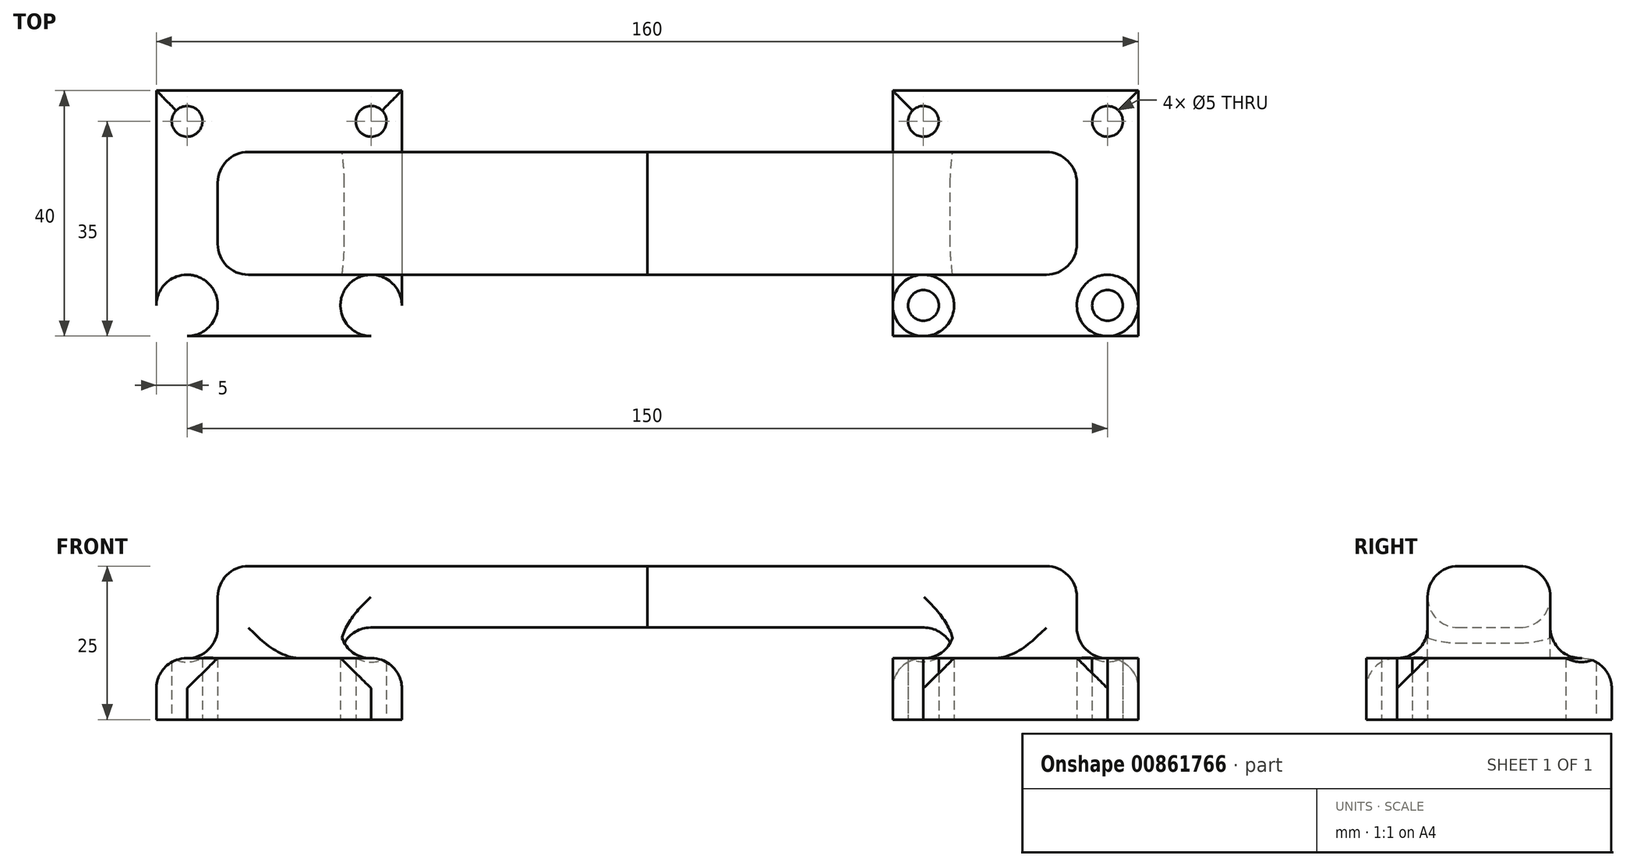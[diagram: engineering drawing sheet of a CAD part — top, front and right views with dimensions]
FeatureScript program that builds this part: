
annotation { "Feature Type Name" : "Feature", "Feature Type Description" : "" }
export const myFeature = defineFeature(function(context is Context, id is Id, definition is map)
    precondition{}
    {
        {
            var Q0;
            Q0=qCreatedBy(makeId("Top.planeOp"),FACE);
            var sketch = newSketch(context, id + "F0", { "sketchPlane" : qUnion([Q0])});
            skLineSegment(sketch, "E0", {"start": v(0, 90.84) * mm, "end": v(0, -111.33) * mm, "construction": true});
            skLineSegment(sketch, "E1.bottom", {"start": v(40, 20) * mm, "end": v(80, 20) * mm});
            skLineSegment(sketch, "E1.top", {"start": v(40, -20) * mm, "end": v(80, -20) * mm});
            skLineSegment(sketch, "E1.left", {"start": v(40, 20) * mm, "end": v(40, -20) * mm});
            skLineSegment(sketch, "E1.right", {"start": v(80, 20) * mm, "end": v(80, -20) * mm});
            skLineSegment(sketch, "E2.bottom", {"start": v(70, -10) * mm, "end": v(50, -10) * mm});
            skLineSegment(sketch, "E2.top", {"start": v(70, 10) * mm, "end": v(50, 10) * mm});
            skLineSegment(sketch, "E2.left", {"start": v(70, -10) * mm, "end": v(70, 10) * mm});
            skLineSegment(sketch, "E2.right", {"start": v(50, -10) * mm, "end": v(50, 10) * mm});
            skLineSegment(sketch, "E3.bottom", {"start": v(70, -10) * mm, "end": v(0, -10) * mm});
            skLineSegment(sketch, "E3.top", {"start": v(70, 10) * mm, "end": v(0, 10) * mm});
            skLineSegment(sketch, "E3.right", {"start": v(0, -10) * mm, "end": v(0, 10) * mm});
            skPoint(sketch, "E4", {"position": v(80, 0) * mm});
            skPoint(sketch, "E5", {"position": v(70, 0) * mm});
            skLineSegment(sketch, "E6", {"start": v(40, 20) * mm, "end": v(50, 10) * mm, "construction": true});
            skLineSegment(sketch, "E7", {"start": v(70, 10) * mm, "end": v(80, 20) * mm, "construction": true});
            skLineSegment(sketch, "E8", {"start": v(70, -10) * mm, "end": v(80, -20) * mm, "construction": true});
            skLineSegment(sketch, "E9", {"start": v(50, -10) * mm, "end": v(40, -20) * mm, "construction": true});
            skPoint(sketch, "E10", {"position": v(75, 15) * mm});
            skPoint(sketch, "E11", {"position": v(45, 15) * mm});
            skPoint(sketch, "E12", {"position": v(45, -15) * mm});
            skPoint(sketch, "E13", {"position": v(75, -15) * mm});
            skCircle(sketch, "E14", {"center": v(45, 15) * mm, "radius": 5 * mm});
            skCircle(sketch, "E15", {"center": v(45, 15) * mm, "radius": 2.5 * mm});
            skCircle(sketch, "E16.MirrorC", {"center": v(75, -15) * mm, "radius": 2.5 * mm});
            skCircle(sketch, "E17.MirrorC", {"center": v(75, -15) * mm, "radius": 5 * mm});
            skLineSegment(sketch, "E18", {"start": v(0, 0) * mm, "end": v(96.53, 0) * mm, "construction": true});
            skCircle(sketch, "E19.MirrorC", {"center": v(45, -15) * mm, "radius": 2.5 * mm});
            skCircle(sketch, "E20.MirrorC", {"center": v(45, -15) * mm, "radius": 5 * mm});
            skCircle(sketch, "E21.MirrorC", {"center": v(75, 15) * mm, "radius": 5 * mm});
            skCircle(sketch, "E22.MirrorC", {"center": v(75, 15) * mm, "radius": 2.5 * mm});
            skSolve(sketch);
        }
        {
            var Q0;
            {var subQ4=sQuery(id+"F0.wireOp",EDGE,"E1.bottom");Q0=makeQuery(id+"F0.imprint","IMPRINT",FACE,{"disambiguationData":[TD([[makeQuery(id+"F0.imprint","IMPRINT",EDGE,{"derivedFrom":subQ4}),-1.0]])]});}
            var Q1;
            {var subQ5=sQuery(id+"F0.wireOp",EDGE,"E2.right");Q1=makeQuery(id+"F0.imprint","IMPRINT",FACE,{"disambiguationData":[TD([[makeQuery(id+"F0.imprint","IMPRINT",EDGE,{"derivedFrom":subQ5}),1.0]])]});}
            var Q2;
            {var subQ0=sQuery(id+"F0.wireOp",EDGE,"E2.right");Q2=makeQuery(id+"F0.imprint","IMPRINT",FACE,{"disambiguationData":[TD([[makeQuery(id+"F0.imprint","IMPRINT",EDGE,{"derivedFrom":subQ0}),-1.0]])]});}
            var Q3;
            {var subQ10=sQuery(id+"F0.wireOp",EDGE,"E2.left");Q3=makeQuery(id+"F0.imprint","IMPRINT",FACE,{"disambiguationData":[TD([[makeQuery(id+"F0.imprint","IMPRINT",EDGE,{"derivedFrom":subQ10}),-1.0]])]});}
            var Q4;
            Q4=makeQuery(id+"F0.imprint","IMPRINT",FACE,{"disambiguationData":[TD([[makeQuery(id+"F0.imprint","IMPRINT",EDGE,{"derivedFrom":sQuery(id+"F0.wireOp",EDGE,"E15")}),-1.0]])]});
            var Q5;
            Q5=makeQuery(id+"F0.imprint","IMPRINT",FACE,{"disambiguationData":[TD([[makeQuery(id+"F0.imprint","IMPRINT",EDGE,{"derivedFrom":sQuery(id+"F0.wireOp",EDGE,"E22.MirrorC")}),-1.0]])]});
            var Q6;
            Q6=makeQuery(id+"F0.imprint","IMPRINT",FACE,{"disambiguationData":[TD([[makeQuery(id+"F0.imprint","IMPRINT",EDGE,{"derivedFrom":sQuery(id+"F0.wireOp",EDGE,"E16.MirrorC")}),1.0]])]});
            var Q7;
            Q7=makeQuery(id+"F0.imprint","IMPRINT",FACE,{"disambiguationData":[TD([[makeQuery(id+"F0.imprint","IMPRINT",EDGE,{"derivedFrom":sQuery(id+"F0.wireOp",EDGE,"E19.MirrorC")}),1.0]])]});
            var Q8;
            {var subQ0=sQuery(id+"F0.wireOp",EDGE,"E3.bottom");var subQ1=sQuery(id+"F0.wireOp",EDGE,"E1.left");var subQ2=makeQuery(id+"F0.imprint","INTERSECT",VERTEX,{"derivedFrom":[subQ1,subQ0]});Q8=makeQuery(id+"F0.imprint","IMPRINT",FACE,{"disambiguationData":[TD([[makeQuery(id+"F0.imprint","IMPRINT",EDGE,{"disambiguationData":[TD([[subQ2,-1.0]])],"derivedFrom":subQ1}),1.0]])]});}
            var Q9;
            {var subQ0=sQuery(id+"F0.wireOp",EDGE,"E14");var subQ1=sQuery(id+"F0.wireOp",EDGE,"E1.left");var subQ2=makeQuery(id+"F0.imprint","INTERSECT",VERTEX,{"derivedFrom":[subQ1,subQ0]});Q9=makeQuery(id+"F0.imprint","IMPRINT",FACE,{"disambiguationData":[TD([[makeQuery(id+"F0.imprint","IMPRINT",EDGE,{"disambiguationData":[TD([[subQ2,-1.0]])],"derivedFrom":subQ1}),1.0]])]});}
            var Q10;
            {var subQ0=sQuery(id+"F0.wireOp",EDGE,"E1.left");var subQ1=sQuery(id+"F0.wireOp",EDGE,"E1.top");var subQ2=makeQuery(id+"F0.imprint","INTERSECT",VERTEX,{"derivedFrom":[subQ1,subQ0]});Q10=makeQuery(id+"F0.imprint","IMPRINT",FACE,{"disambiguationData":[TD([[makeQuery(id+"F0.imprint","IMPRINT",EDGE,{"disambiguationData":[TD([[subQ2,-1.0]])],"derivedFrom":subQ1}),1.0]])]});}
            var Q11;
            {var subQ0=sQuery(id+"F0.wireOp",EDGE,"E1.right");var subQ1=sQuery(id+"F0.wireOp",EDGE,"E1.top");var subQ2=makeQuery(id+"F0.imprint","INTERSECT",VERTEX,{"derivedFrom":[subQ1,subQ0]});Q11=makeQuery(id+"F0.imprint","IMPRINT",FACE,{"disambiguationData":[TD([[makeQuery(id+"F0.imprint","IMPRINT",EDGE,{"disambiguationData":[TD([[subQ2,1.0]])],"derivedFrom":subQ1}),1.0]])]});}
            extrude(context, id + "F1", {"entities" : qUnion([Q0, Q1, Q2, Q3, Q4, Q5, Q6, Q7, Q8, Q9, Q10, Q11]), "depth" : 10 * mm, "offsetDistance" : 25 * mm});
        }
        {
            var Q0;
            {var subQ0=sQuery(id+"F0.wireOp",EDGE,"E2.right");Q0=makeQuery(id+"F0.imprint","IMPRINT",FACE,{"disambiguationData":[TD([[makeQuery(id+"F0.imprint","IMPRINT",EDGE,{"derivedFrom":subQ0}),-1.0]])]});}
            extrude(context, id + "F2", {"entities" : qUnion([Q0]), "operationType" : NewBodyOperationType.ADD, "depth" : 25 * mm, "offsetDistance" : 25 * mm});
        }
        {
            var Q0;
            {var subQ5=sQuery(id+"F0.wireOp",EDGE,"E3.right");Q0=makeQuery(id+"F0.imprint","IMPRINT",FACE,{"disambiguationData":[TD([[makeQuery(id+"F0.imprint","IMPRINT",EDGE,{"derivedFrom":subQ5}),-1.0]])]});}
            var Q1;
            {var subQ5=sQuery(id+"F0.wireOp",EDGE,"E2.right");Q1=makeQuery(id+"F0.imprint","IMPRINT",FACE,{"disambiguationData":[TD([[makeQuery(id+"F0.imprint","IMPRINT",EDGE,{"derivedFrom":subQ5}),1.0]])]});}
            var Q2;
            {var subQ0=sQuery(id+"F0.wireOp",EDGE,"E2.right");Q2=makeQuery(id+"F0.imprint","IMPRINT",FACE,{"disambiguationData":[TD([[makeQuery(id+"F0.imprint","IMPRINT",EDGE,{"derivedFrom":subQ0}),-1.0]])]});}
            extrude(context, id + "F3", {"entities" : qUnion([Q0, Q1, Q2]), "operationType" : NewBodyOperationType.ADD, "depth" : 25 * mm, "offsetDistance" : 25 * mm, "hasSecondDirection" : true, "secondDirectionOppositeDirection" : false, "secondDirectionDepth" : 15 * mm});
        }
        {
            var Q0;
            Q0=makeQuery(id+"F2.opExtrude","CAP_EDGE",EDGE,{"disambiguationData":[OSD([sQuery(id+"F0.wireOp",EDGE,"E2.left")])],"isStart":false});
            var Q1;
            Q1=makeQuery(id+"F3.opExtrude","CAP_EDGE",EDGE,{"disambiguationData":[OSD([sQuery(id+"F0.wireOp",EDGE,"E3.bottom")])],"isStart":true});
            var Q2;
            Q2=makeQuery(id+"F3.opExtrude","CAP_EDGE",EDGE,{"disambiguationData":[OSD([sQuery(id+"F0.wireOp",EDGE,"E3.top")])],"isStart":true});
            var Q3;
            {var subQ0=sQuery(id+"F0.wireOp",EDGE,"E3.top");Q3=makeQuery(id+"F3.boolean.opBoolean","MERGE",EDGE,{"derivedFrom":[makeQuery(id+"F2.opExtrude","CAP_EDGE",EDGE,{"disambiguationData":[OSD([subQ0])],"isStart":false}),makeQuery(id+"F3.opExtrude","CAP_EDGE",EDGE,{"disambiguationData":[OSD([subQ0])],"isStart":false})]});}
            var Q4;
            {var subQ0=sQuery(id+"F0.wireOp",EDGE,"E3.bottom");Q4=makeQuery(id+"F3.boolean.opBoolean","MERGE",EDGE,{"derivedFrom":[makeQuery(id+"F2.opExtrude","CAP_EDGE",EDGE,{"disambiguationData":[OSD([subQ0])],"isStart":false}),makeQuery(id+"F3.opExtrude","CAP_EDGE",EDGE,{"disambiguationData":[OSD([subQ0])],"isStart":false})]});}
            var Q5;
            Q5=makeQuery(id+"F2.opExtrude","SWEPT_FACE",FACE,{"disambiguationData":[OSD([sQuery(id+"F0.wireOp",EDGE,"E2.left")])]});
            fillet(context, id + "F4", {"entities" : qUnion([Q0, Q1, Q2, Q3, Q4, Q5]), "radius" : 5 * mm, "tangentPropagation" : true, "allowEdgeOverflow" : false});
        }
        {
            var Q0;
            Q0=makeQuery(id+"F1.opExtrude","CAP_EDGE",EDGE,{"disambiguationData":[OSD([sQuery(id+"F0.wireOp",EDGE,"E1.bottom")])],"isStart":false});
            var Q1;
            Q1=makeQuery(id+"F1.opExtrude","CAP_EDGE",EDGE,{"disambiguationData":[OSD([sQuery(id+"F0.wireOp",EDGE,"E1.left")])],"isStart":false});
            var Q2;
            Q2=makeQuery(id+"F1.opExtrude","CAP_EDGE",EDGE,{"disambiguationData":[OSD([sQuery(id+"F0.wireOp",EDGE,"E1.right")])],"isStart":false});
            var Q3;
            Q3=makeQuery(id+"F1.opExtrude","CAP_EDGE",EDGE,{"disambiguationData":[OSD([sQuery(id+"F0.wireOp",EDGE,"E1.top")])],"isStart":false});
            var Q4;
            Q4=makeQuery(id+"F2.boolean.opBoolean","INTERSECT",EDGE,{"derivedFrom":[makeQuery(id+"F1.opExtrude","CAP_FACE",FACE,{"disambiguationData":[OSD([sQuery(id+"F0.wireOp",EDGE,"E1.bottom"),sQuery(id+"F0.wireOp",EDGE,"E1.top"),sQuery(id+"F0.wireOp",EDGE,"E1.left"),sQuery(id+"F0.wireOp",EDGE,"E1.right"),sQuery(id+"F0.wireOp",EDGE,"E15"),sQuery(id+"F0.wireOp",EDGE,"E16.MirrorC"),sQuery(id+"F0.wireOp",EDGE,"E19.MirrorC"),sQuery(id+"F0.wireOp",EDGE,"E22.MirrorC")])],"isStart":false}),makeQuery(id+"F2.opExtrude","SWEPT_FACE",FACE,{"disambiguationData":[OSD([sQuery(id+"F0.wireOp",EDGE,"E2.right")])]})]});
            var Q5;
            Q5=makeQuery(id+"F3.boolean.opBoolean","INTERSECT",EDGE,{"derivedFrom":[makeQuery(id+"F2.opExtrude","SWEPT_FACE",FACE,{"disambiguationData":[OSD([sQuery(id+"F0.wireOp",EDGE,"E2.right")])]}),makeQuery(id+"F3.opExtrude","CAP_FACE",FACE,{"disambiguationData":[OSD([sQuery(id+"F0.wireOp",EDGE,"E3.bottom"),sQuery(id+"F0.wireOp",EDGE,"E3.top"),sQuery(id+"F0.wireOp",EDGE,"E2.left"),sQuery(id+"F0.wireOp",EDGE,"E3.right")])],"isStart":true})]});
            var Q6;
            Q6=makeQuery(id+"F4.opFillet","BLEND_EDGE",EDGE,{"blendedFrom":[makeQuery(id+"F3.opExtrude","CAP_EDGE",EDGE,{"disambiguationData":[OSD([sQuery(id+"F0.wireOp",EDGE,"E3.top")])],"isStart":true}),makeQuery(id+"F2.opExtrude","SWEPT_FACE",FACE,{"disambiguationData":[OSD([sQuery(id+"F0.wireOp",EDGE,"E2.right")])]})],"blendedInto":[makeQuery(id+"F2.opExtrude","SWEPT_FACE",FACE,{"disambiguationData":[OSD([sQuery(id+"F0.wireOp",EDGE,"E2.right")])]})]});
            fillet(context, id + "F5", {"entities" : qUnion([Q0, Q1, Q2, Q3, Q4, Q5, Q6]), "radius" : 4.9 * mm, "tangentPropagation" : true, "allowEdgeOverflow" : false});
        }
        {
            var Q0;
            Q0=makeQuery(id+"F1.opExtrude","SWEPT_BODY",BODY,{"disambiguationData":[OSD([sQuery(id+"F0.wireOp",EDGE,"E1.bottom"),sQuery(id+"F0.wireOp",EDGE,"E1.top"),sQuery(id+"F0.wireOp",EDGE,"E1.left"),sQuery(id+"F0.wireOp",EDGE,"E1.right")])]});
            var Q1;
            Q1=makeQuery(id+"F3.opExtrude","SWEPT_FACE",FACE,{"disambiguationData":[OSD([sQuery(id+"F0.wireOp",EDGE,"E3.right")])]});
            mirror(context, id + "F6", {"operationType" : NewBodyOperationType.ADD, "entities" : qUnion([Q0]), "mirrorPlane" : qUnion([Q1])});
        }
    });
